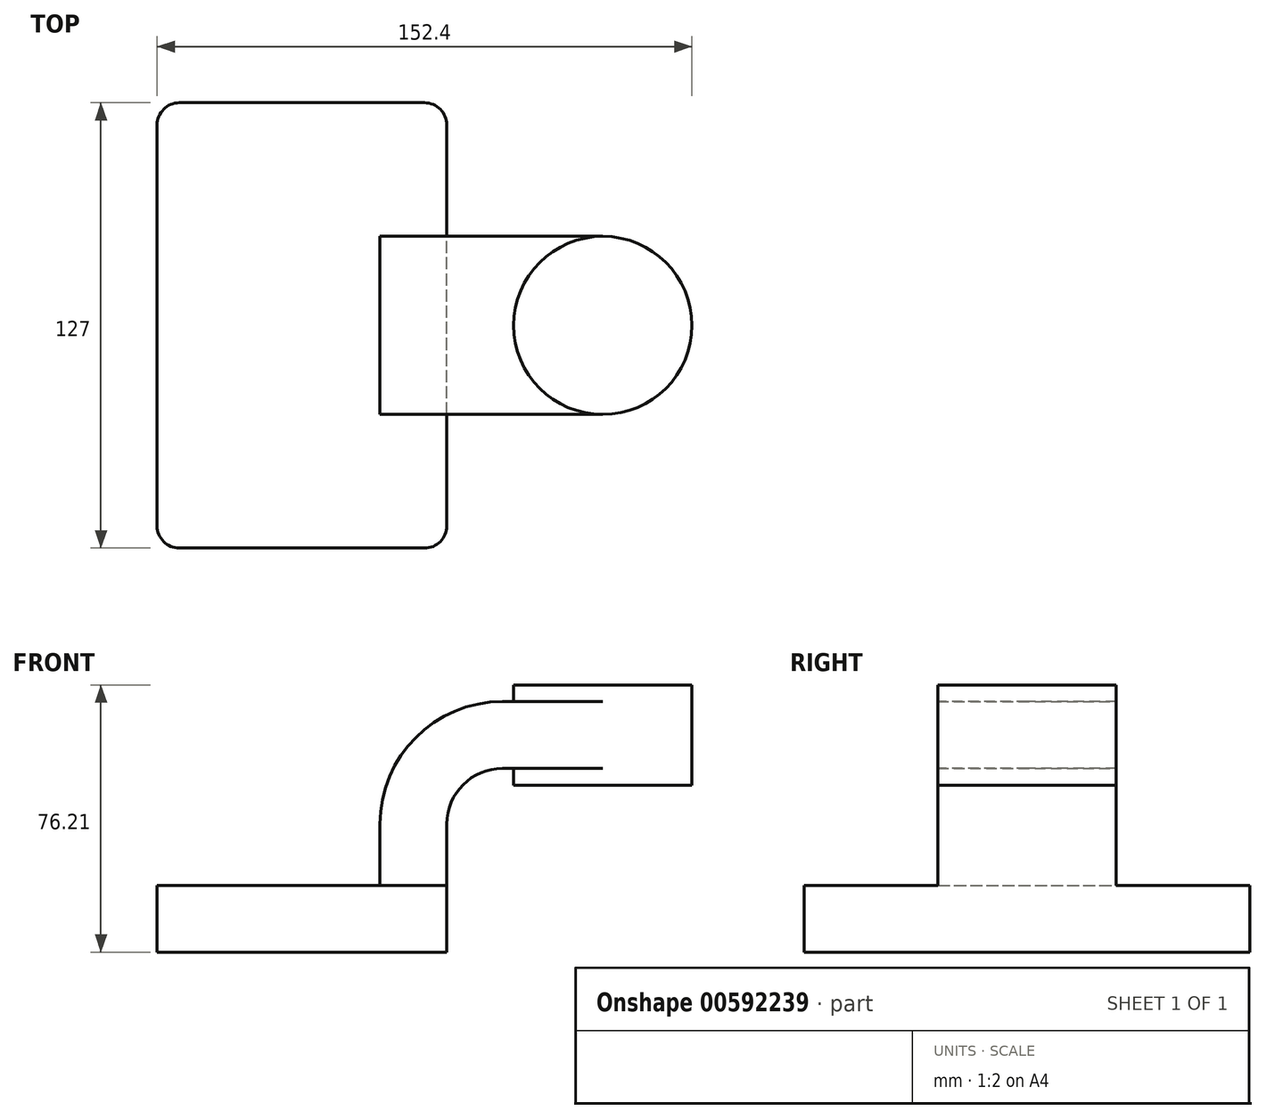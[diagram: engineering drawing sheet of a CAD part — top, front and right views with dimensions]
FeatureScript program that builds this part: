
annotation { "Feature Type Name" : "Feature", "Feature Type Description" : "" }
export const myFeature = defineFeature(function(context is Context, id is Id, definition is map)
    precondition{}
    {
        {
            var Q0;
            Q0=qCreatedBy(makeId("Front.planeOp"),FACE);
            var sketch = newSketch(context, id + "F0", { "sketchPlane" : qUnion([Q0])});
            skLineSegment(sketch, "E0.bottom", {"start": v(41.27, 9.53) * mm, "end": v(-41.28, 9.53) * mm});
            skLineSegment(sketch, "E0.top", {"start": v(41.28, -9.52) * mm, "end": v(-41.27, -9.52) * mm});
            skLineSegment(sketch, "E0.left", {"start": v(41.28, 9.53) * mm, "end": v(41.28, -9.52) * mm});
            skLineSegment(sketch, "E0.right", {"start": v(-41.28, 9.53) * mm, "end": v(-41.27, -9.52) * mm});
            skPoint(sketch, "E0.middle", {"position": v(0, 0) * mm});
            skLineSegment(sketch, "E1.bottom", {"start": v(111.12, 66.67) * mm, "end": v(60.33, 66.67) * mm});
            skLineSegment(sketch, "E1.top", {"start": v(111.13, 38.1) * mm, "end": v(60.33, 38.1) * mm});
            skLineSegment(sketch, "E1.left", {"start": v(111.13, 66.68) * mm, "end": v(111.13, 38.1) * mm});
            skLineSegment(sketch, "E1.right", {"start": v(60.33, 66.68) * mm, "end": v(60.33, 38.1) * mm});
            skPoint(sketch, "E1.middle", {"position": v(85.73, 52.39) * mm});
            skLineSegment(sketch, "E2", {"start": v(41.27, 9.53) * mm, "end": v(41.27, 26.99) * mm});
            skArc(sketch, "E3", {"start": v(41.28, 26.99) * mm, "mid": v(45.92, 38.21) * mm, "end": v(57.15, 42.86) * mm});
            skLineSegment(sketch, "E4", {"start": v(57.15, 42.86) * mm, "end": v(85.73, 42.86) * mm});
            skPoint(sketch, "E4.endSnap0", {"position": v(85.73, 38.1) * mm});
            skLineSegment(sketch, "E5.0", {"start": v(57.15, 61.91) * mm, "end": v(85.73, 61.91) * mm});
            skArc(sketch, "E5.1", {"start": v(22.23, 26.99) * mm, "mid": v(32.45, 51.68) * mm, "end": v(57.15, 61.91) * mm});
            skLineSegment(sketch, "E5.2", {"start": v(22.22, 9.53) * mm, "end": v(22.22, 26.99) * mm});
            skLineSegment(sketch, "E6", {"start": v(85.73, 38.1) * mm, "end": v(85.73, 66.68) * mm});
            skFitSpline(sketch, "E7", {"points": [v(57.15, 61.91) * mm, v(-41.28, 9.53) * mm], "startDerivative": vector(-171.45, 0) * mm, "endDerivative": vector(0, -92.36) * mm});
            skSolve(sketch);
        }
        {
            var Q0;
            Q0=makeQuery(id+"F0.imprint","IMPRINT",FACE,{"disambiguationData":[TD([[makeQuery(id+"F0.imprint","IMPRINT",EDGE,{"derivedFrom":sQuery(id+"F0.wireOp",EDGE,"E0.top")}),-1.0]])]});
            extrude(context, id + "F1", {"entities" : qUnion([Q0]), "endBound" : BoundingType.SYMMETRIC, "depth" : 127 * mm, "offsetDistance" : 25.4 * mm});
        }
        {
            var Q0;
            {var subQ0=sQuery(id+"F0.wireOp",EDGE,"E5.0");var subQ1=sQuery(id+"F0.wireOp",EDGE,"E1.right");var subQ2=makeQuery(id+"F0.imprint","INTERSECT",VERTEX,{"derivedFrom":[subQ1,subQ0]});Q0=makeQuery(id+"F0.imprint","IMPRINT",FACE,{"disambiguationData":[TD([[makeQuery(id+"F0.imprint","IMPRINT",EDGE,{"disambiguationData":[TD([[subQ2,-1.0]])],"derivedFrom":subQ1}),1.0]])]});}
            var Q1;
            {var subQ1=sQuery(id+"F0.wireOp",EDGE,"E2");Q1=makeQuery(id+"F0.imprint","IMPRINT",FACE,{"disambiguationData":[TD([[makeQuery(id+"F0.imprint","IMPRINT",EDGE,{"derivedFrom":subQ1}),1.0]])]});}
            extrude(context, id + "F2", {"entities" : qUnion([Q0, Q1]), "operationType" : NewBodyOperationType.ADD, "endBound" : BoundingType.SYMMETRIC, "depth" : 50.8 * mm, "offsetDistance" : 25.4 * mm});
        }
        {
            var Q0;
            Q0=makeQuery(id+"F0.imprint","IMPRINT",FACE,{"disambiguationData":[TD([[makeQuery(id+"F0.imprint","IMPRINT",EDGE,{"derivedFrom":sQuery(id+"F0.wireOp",EDGE,"E5.1")}),1.0]])]});
            extrude(context, id + "F3", {"entities" : qUnion([Q0]), "operationType" : NewBodyOperationType.ADD, "endBound" : BoundingType.SYMMETRIC, "depth" : 15.88 * mm, "offsetDistance" : 25.4 * mm});
        }
        {
            var Q0;
            {var subQ4=sQuery(id+"F0.wireOp",EDGE,"E1.left");Q0=makeQuery(id+"F0.imprint","IMPRINT",FACE,{"disambiguationData":[TD([[makeQuery(id+"F0.imprint","IMPRINT",EDGE,{"derivedFrom":subQ4}),-1.0]])]});}
            var Q1;
            Q1=sQuery(id+"F0.wireOp",EDGE,"E6");
            revolve(context, id + "F4", {"operationType" : NewBodyOperationType.ADD, "entities" : qUnion([Q0]), "axis" : qUnion([Q1]), "revolveType" : RevolveType.FULL});
        }
        {
            var Q0;
            Q0=makeQuery(id+"F1.opExtrude","CAP_EDGE",EDGE,{"disambiguationData":[OSD([sQuery(id+"F0.wireOp",EDGE,"E0.left")])],"isStart":false});
            var Q1;
            Q1=makeQuery(id+"F1.opExtrude","CAP_EDGE",EDGE,{"disambiguationData":[OSD([sQuery(id+"F0.wireOp",EDGE,"E0.left")])],"isStart":true});
            var Q2;
            Q2=makeQuery(id+"F1.opExtrude","CAP_EDGE",EDGE,{"disambiguationData":[OSD([sQuery(id+"F0.wireOp",EDGE,"E0.right")])],"isStart":true});
            var Q3;
            Q3=makeQuery(id+"F1.opExtrude","CAP_EDGE",EDGE,{"disambiguationData":[OSD([sQuery(id+"F0.wireOp",EDGE,"E0.right")])],"isStart":false});
            fillet(context, id + "F5", {"entities" : qUnion([Q0, Q1, Q2, Q3]), "radius" : 6.35 * mm, "tangentPropagation" : true, "allowEdgeOverflow" : false});
        }
    });
